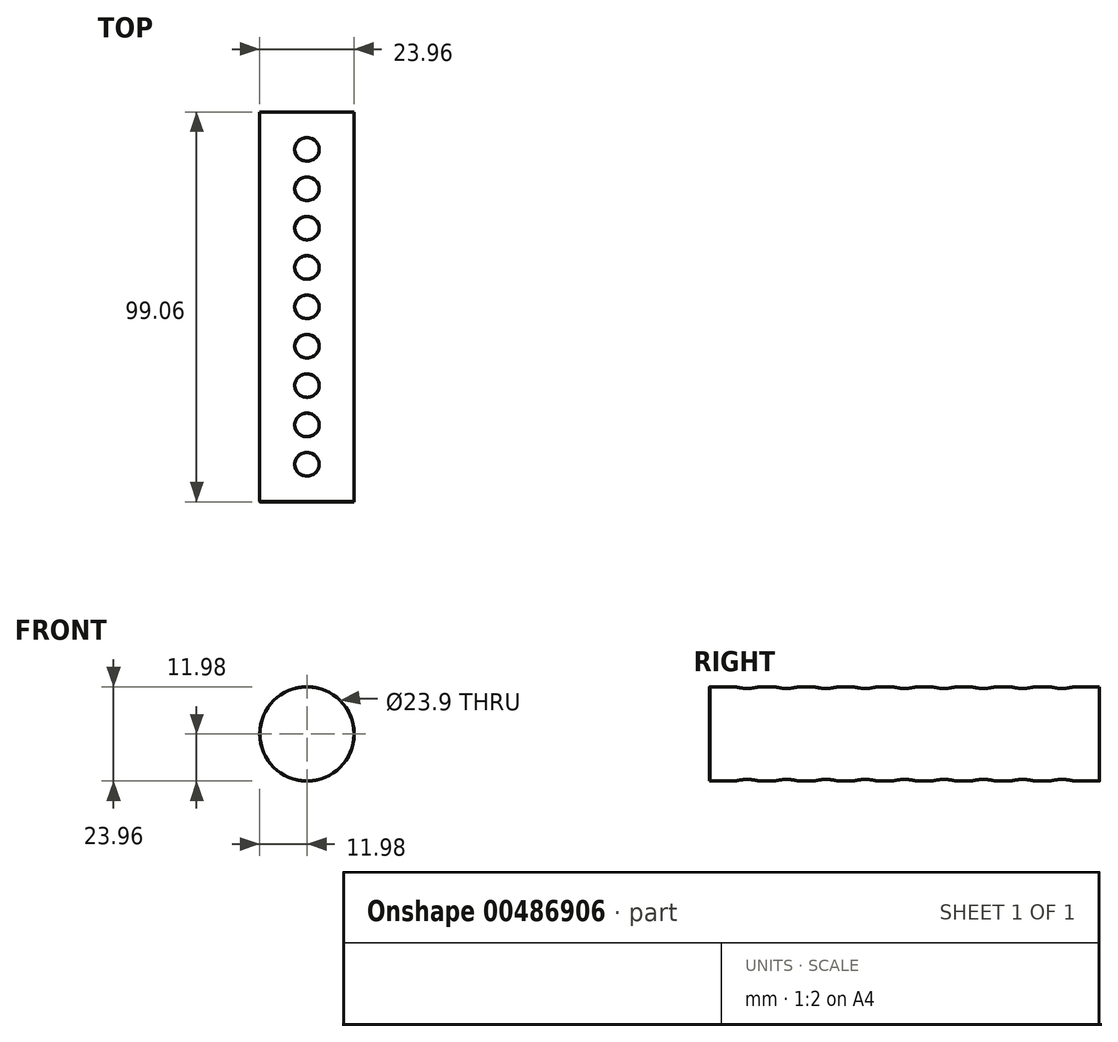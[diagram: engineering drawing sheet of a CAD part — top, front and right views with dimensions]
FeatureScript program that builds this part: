
annotation { "Feature Type Name" : "Feature", "Feature Type Description" : "" }
export const myFeature = defineFeature(function(context is Context, id is Id, definition is map)
    precondition{}
    {
        {
            var Q0;
            Q0=qCreatedBy(makeId("Front.planeOp"),FACE);
            var sketch = newSketch(context, id + "F0", { "sketchPlane" : qUnion([Q0])});
            skCircle(sketch, "E0", {"center": v(0, 0) * mm, "radius": 11.97 * mm});
            skCircle(sketch, "E1", {"center": v(0, 0) * mm, "radius": 11.95 * mm});
            skSolve(sketch);
        }
        {
            var Q0;
            Q0 = qSketchRegion(id + "F0", true);
            extrude(context, id + "F1", {"entities" : qUnion([Q0]), "depth" : 100 * mm});
        }
        {
            var Q0;
            Q0=qCreatedBy(makeId("Top.planeOp"),FACE);
            var sketch = newSketch(context, id + "F2", { "sketchPlane" : qUnion([Q0])});
            skCircle(sketch, "E2", {"center": v(0, -10) * mm, "radius": 2.5 * mm});
            skCircle(sketch, "E3", {"center": v(0, -20) * mm, "radius": 2.5 * mm});
            skCircle(sketch, "E4", {"center": v(0, -30) * mm, "radius": 2.5 * mm});
            skCircle(sketch, "E5", {"center": v(0, -40) * mm, "radius": 2.5 * mm});
            skCircle(sketch, "E6", {"center": v(0, -50) * mm, "radius": 2.5 * mm});
            skCircle(sketch, "E7", {"center": v(0, -60) * mm, "radius": 2.5 * mm});
            skCircle(sketch, "E8", {"center": v(0, -70) * mm, "radius": 2.5 * mm});
            skCircle(sketch, "E9", {"center": v(0, -90) * mm, "radius": 2.5 * mm});
            skCircle(sketch, "E10", {"center": v(0, -80) * mm, "radius": 2.5 * mm});
            skSolve(sketch);
        }
        {
            var Q0;
            Q0 = qSketchRegion(id + "F2", true);
            extrude(context, id + "F3", {"entities" : qUnion([Q0]), "operationType" : NewBodyOperationType.REMOVE, "endBound" : BoundingType.SYMMETRIC, "oppositeDirection" : true, "depth" : 25 * mm});
        }
        {
            var Q0;
            Q0=makeQuery(id+"F1.opExtrude","SWEPT_FACE",FACE,{"disambiguationData":[OSD([sQuery(id+"F0.wireOp",EDGE,"E0")])]});
            chamfer(context, id + "F4", {"entities" : qUnion([Q0]), "width" : 0.5 * mm, "tangentPropagation" : true});
        }
    });
